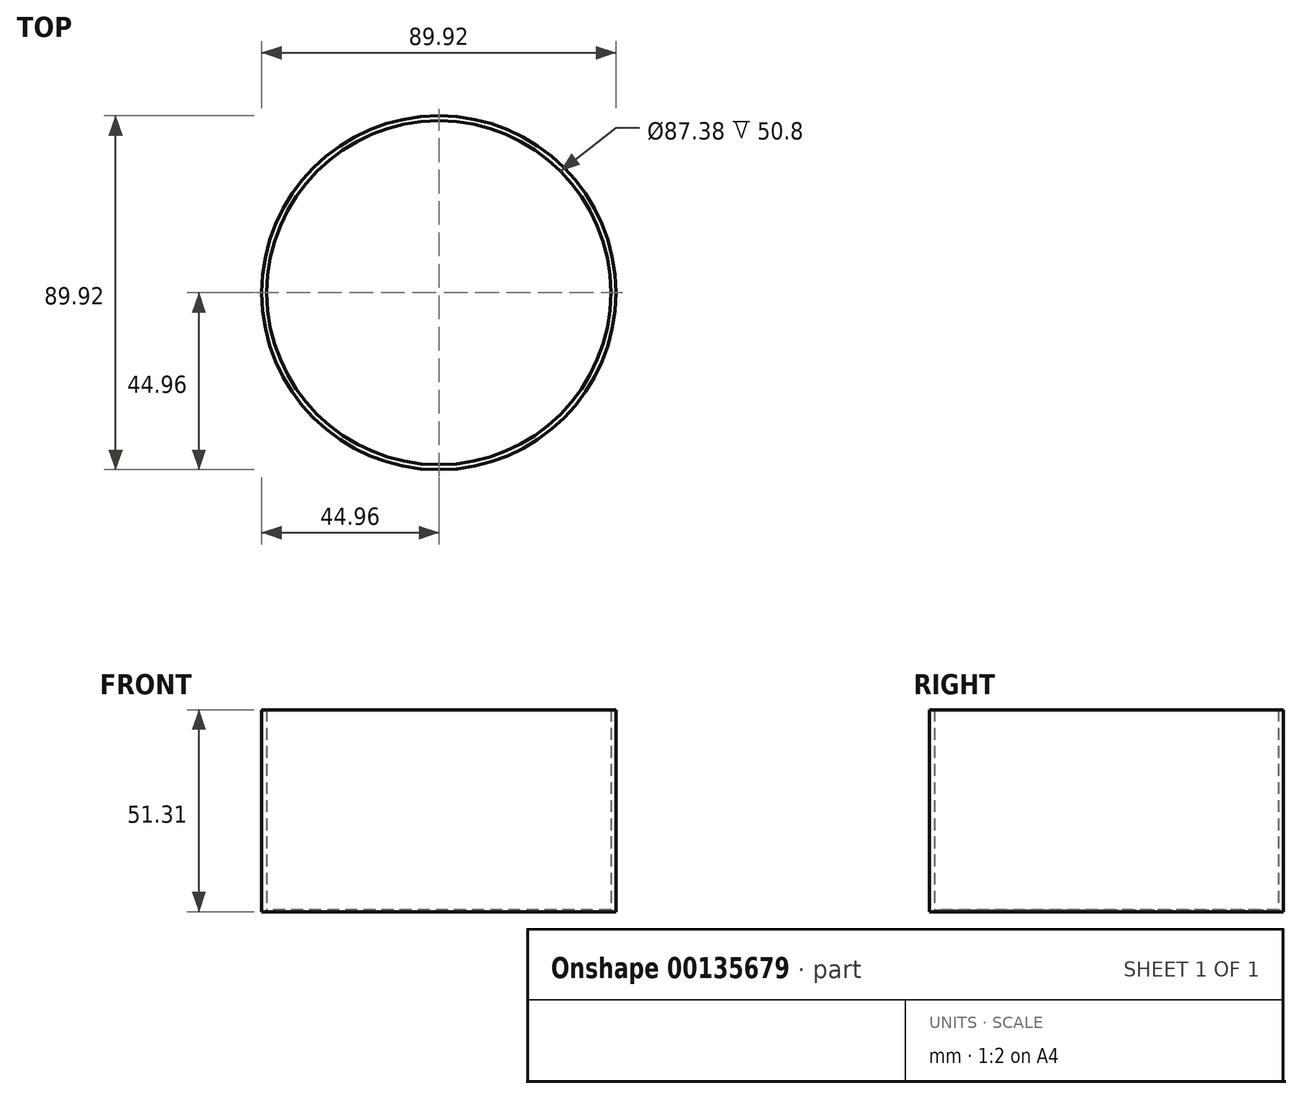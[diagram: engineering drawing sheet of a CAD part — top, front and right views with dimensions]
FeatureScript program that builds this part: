
annotation { "Feature Type Name" : "Feature", "Feature Type Description" : "" }
export const myFeature = defineFeature(function(context is Context, id is Id, definition is map)
    precondition{}
    {
        {
            var Q0;
            Q0=qCreatedBy(makeId("Top.planeOp"),FACE);
            var sketch = newSketch(context, id + "F0", { "sketchPlane" : qUnion([Q0])});
            skCircle(sketch, "E0", {"center": v(0, 0) * mm, "radius": 44.96 * mm});
            skSolve(sketch);
        }
        {
            var Q0;
            Q0=sQuery(id+"F0.wireOp",EDGE,"E0");
            extrude(context, id + "F1", {"bodyType" : ToolBodyType.SURFACE, "surfaceEntities" : qUnion([Q0]), "depth" : 50.8 * mm});
        }
        {
            var Q0;
            Q0=qCreatedBy(makeId("Top.planeOp"),FACE);
            var sketch = newSketch(context, id + "F2", { "sketchPlane" : qUnion([Q0])});
            skCircle(sketch, "E1", {"center": v(0, 0) * mm, "radius": 44.96 * mm});
            skSolve(sketch);
        }
        {
            var Q0;
            Q0=qSketchRegion(id+"F2",true);
            extrude(context, id + "F3", {"entities" : qUnion([Q0]), "oppositeDirection" : true, "depth" : 0.5 * mm});
        }
        {
            var Q0;
            Q0=qCreatedBy(makeId("Top.planeOp"),FACE);
            var sketch = newSketch(context, id + "F4", { "sketchPlane" : qUnion([Q0])});
            skCircle(sketch, "E2", {"center": v(0, 0) * mm, "radius": 44.96 * mm});
            skCircle(sketch, "E3", {"center": v(0, 0) * mm, "radius": 43.69 * mm});
            skSolve(sketch);
        }
        {
            var Q0;
            Q0=qSketchRegion(id+"F4",true);
            extrude(context, id + "F5", {"entities" : qUnion([Q0]), "operationType" : NewBodyOperationType.ADD, "depth" : 50.8 * mm});
        }
    });
